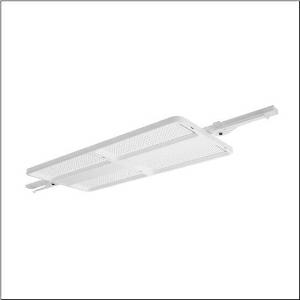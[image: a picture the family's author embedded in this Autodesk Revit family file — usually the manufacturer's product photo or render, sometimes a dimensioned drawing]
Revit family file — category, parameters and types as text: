
# Revit family: highbay_11_fur_modario_r__tragschiene_maxi_51hn12db4wma_d53a
name_source: partatom
category: Lighting Fixtures
units: mm (PartAtom-declared; Revit-internal decimal feet)

## family parameters
Cut with Voids When Loaded = No
Host = Face
Light Source = No
Part Type = Normal
Room Calculation Point = No
Round Connector Dimension = Use Diameter
Shared = No

## types (1)
- --- (1 x LED, 63000 lm, 329.9 W, 4000K)
    Apparent Load = 330 VA
    CIE Flux Codes = 87 98 100 100 100
    Color Rendering = 80
    Color Temperature = 4000K
    Default Elevation = 1800 mm
    Description = high bay luminaire Highbay 11 for Modario® trunking rail maxi; direct symmetric wide distribution, light control with lens of PMMA; UGR ≤ 22 (X = 4H | Y = 8H | S = 0.25H | reflection values 70/50/20); luminous flux: 63.000lm; light colour: 840, colour temperature: 4000K, MacAdam ≤ 2 SDCM (initial), colour rendering: CRI > 80; luminous efficacy: 191lm/W; rated service life: 100.000h (L95/B50) at AT= 25°C; control: DALI 2; luminaire connection: plug, 5-pole, with phase selectionmains connection: 230..240V, AC 50/60Hz; connected load: 329,9W; protection rating (complete): IP64; insulation class (complete): insulation class I (protective earthing); protection symbol: D; impact resistance: IK07; certification: CE, ENEC, VDE, UKCA; internal wiring halogen-free; luminaire LABS conformity tested according to VDMA 24364:2018-05; corresponds to IFS (International Featured Standards) requirements for safety and quality in the food industry; housing frame of high-performance plastic PA6, matt traffic white (RAL 9016); cover of PMMA; fixing on rail side of steel, galvanised, white; blank cover of PC, traffic white (RAL 9016); dimension (LxWxH): 1.496 x 442 x 72mm; permissible operating ambient temperature: -40..+45°C (reducing of maximum allowable ambient temperature of 5°C with ceiling mounting); packaging unit: 1 piece
    Height = 72 mm  [stored 0.23622 ft]
    Lamp = 1 x LED
    Lamp Light Flux = 63000 lm
    Lamp Power = 329.9 W
    Lamp count = 1
    Length = 946 mm
    Luminous efficacy = 191 lm/W
    Manufacturer = Siteco
    ModVariant = No
    Model = 51HN12DB4WMA
    Mounting Place = Ceiling
    Mounting Type = Pendant
    Number of Poles = 1
    OnlyDefault = Yes
    Power Factor = 1
    Product Name = Highbay 11 für Modario® Tragschiene maxi
    Product group = high bay luminaire
    ProductGroupID = 901
    Protection Class = Protection class I
    Protection Degree = IP 64
    RLX_Detail_Level = 1
    RLX_Emergency_Light_Flux = 0 lm
    RLX_Emergency_Type = 0
    RLX_Emergency_Type_DB = No
    RlxData = <blob elided: 21329 chars, md5=3a3043de>
    Socket = socket
    Standby Power = 0 W
    System Light Flux = 63001 lm
    System Power = 330 W
    Type Comments = factory setting: luminous flux: 100 % | dim-lin: 254 | 745 mA
    Type Image = l_1363248.jpg
    URL = http://relux.com
    VarID = @adj_014457
    Voltage = 0 V
    Weight = 0.00 kg
    Width = 442 mm

note: [stored X ft] marks values corroborated as IEEE doubles in the binary element streams (Revit-internal decimal feet)

## geometry (parser evidence)
native form markers: Blend x4, Sweep x12
no freeform markers — native parametric forms only
